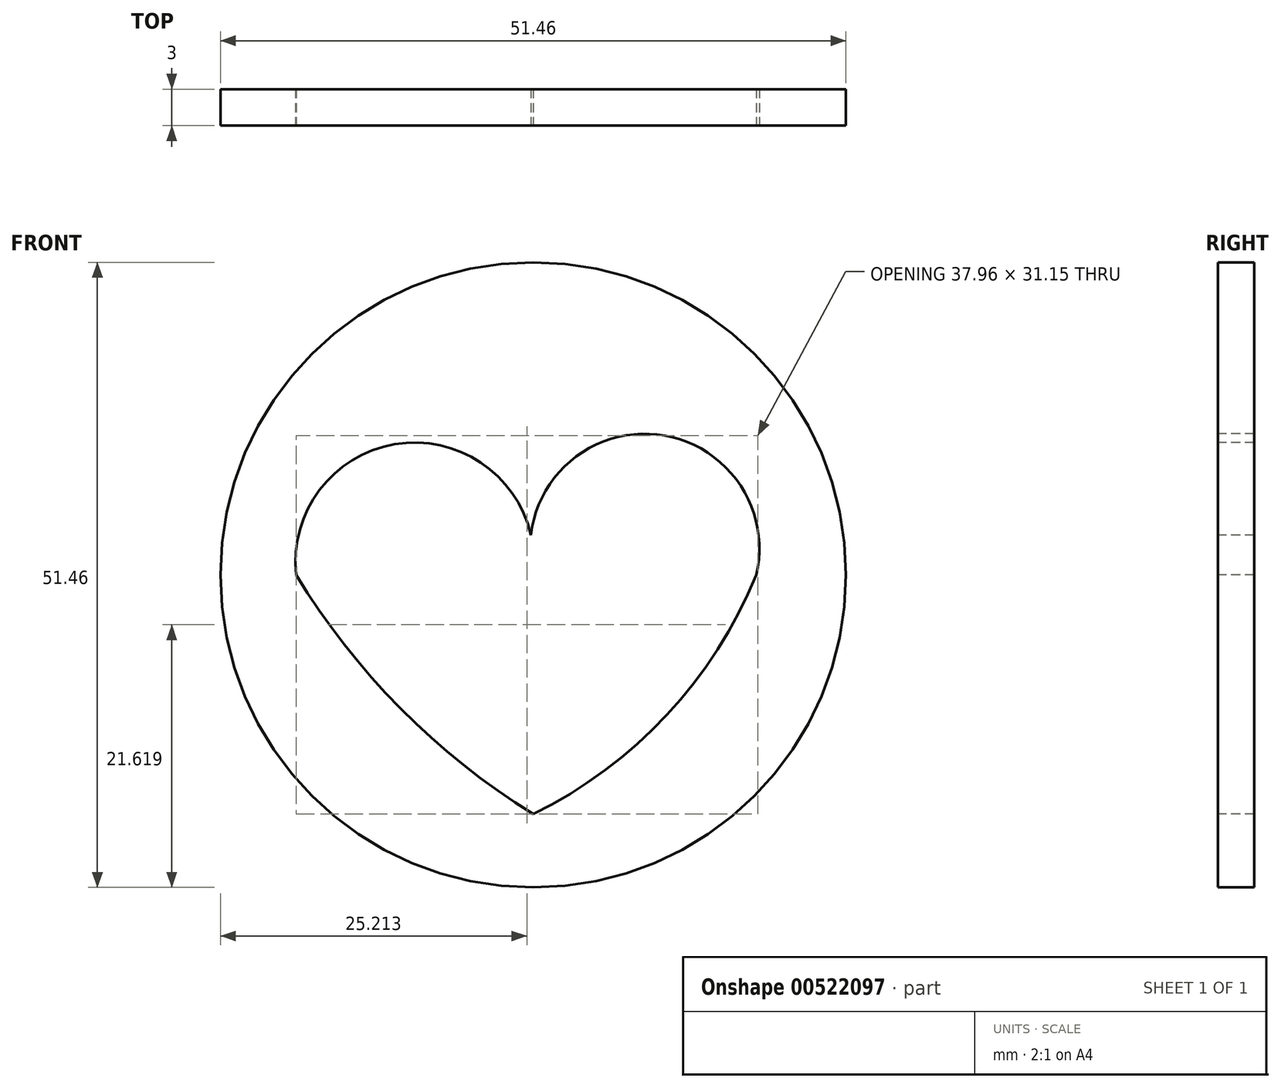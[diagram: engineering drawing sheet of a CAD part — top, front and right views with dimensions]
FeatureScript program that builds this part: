
annotation { "Feature Type Name" : "Feature", "Feature Type Description" : "" }
export const myFeature = defineFeature(function(context is Context, id is Id, definition is map)
    precondition{}
    {
        {
            var Q0;
            Q0=qCreatedBy(makeId("Front.planeOp"),FACE);
            var sketch = newSketch(context, id + "F0", { "sketchPlane" : qUnion([Q0])});
            skCircle(sketch, "E0", {"center": v(0, 0) * mm, "radius": 25.73 * mm});
            skSolve(sketch);
        }
        {
            var Q0;
            Q0 = qSketchRegion(id + "F0", true);
            extrude(context, id + "F1", {"entities" : qUnion([Q0]), "depth" : 3 * mm, "offsetDistance" : 25 * mm});
        }
        {
            var Q0;
            Q0=makeQuery(id+"F1.opExtrude","CAP_FACE",FACE,{"disambiguationData":[OSD([sQuery(id+"F0.wireOp",EDGE,"E0")])],"isStart":false});
            var sketch = newSketch(context, id + "F2", { "sketchPlane" : qUnion([Q0])});
            skArc(sketch, "E1", {"start": v(18.35, 0) * mm, "mid": v(9.17, 11.61) * mm, "end": v(0, 0) * mm});
            skArc(sketch, "E2", {"start": v(0, 0) * mm, "mid": v(-9.75, 10.89) * mm, "end": v(-19.5, 0) * mm});
            skArc(sketch, "E3", {"start": v(-19.5, 0) * mm, "mid": v(-10.9, -11) * mm, "end": v(0, -19.69) * mm});
            skArc(sketch, "E4", {"start": v(0, -19.69) * mm, "mid": v(10.99, -11.53) * mm, "end": v(18.35, 0) * mm});
            skSolve(sketch);
        }
        {
            var Q0;
            Q0 = qSketchRegion(id + "F2", true);
            extrude(context, id + "F3", {"entities" : qUnion([Q0]), "operationType" : NewBodyOperationType.REMOVE, "oppositeDirection" : true, "depth" : 25 * mm, "offsetDistance" : 25 * mm});
        }
    });
